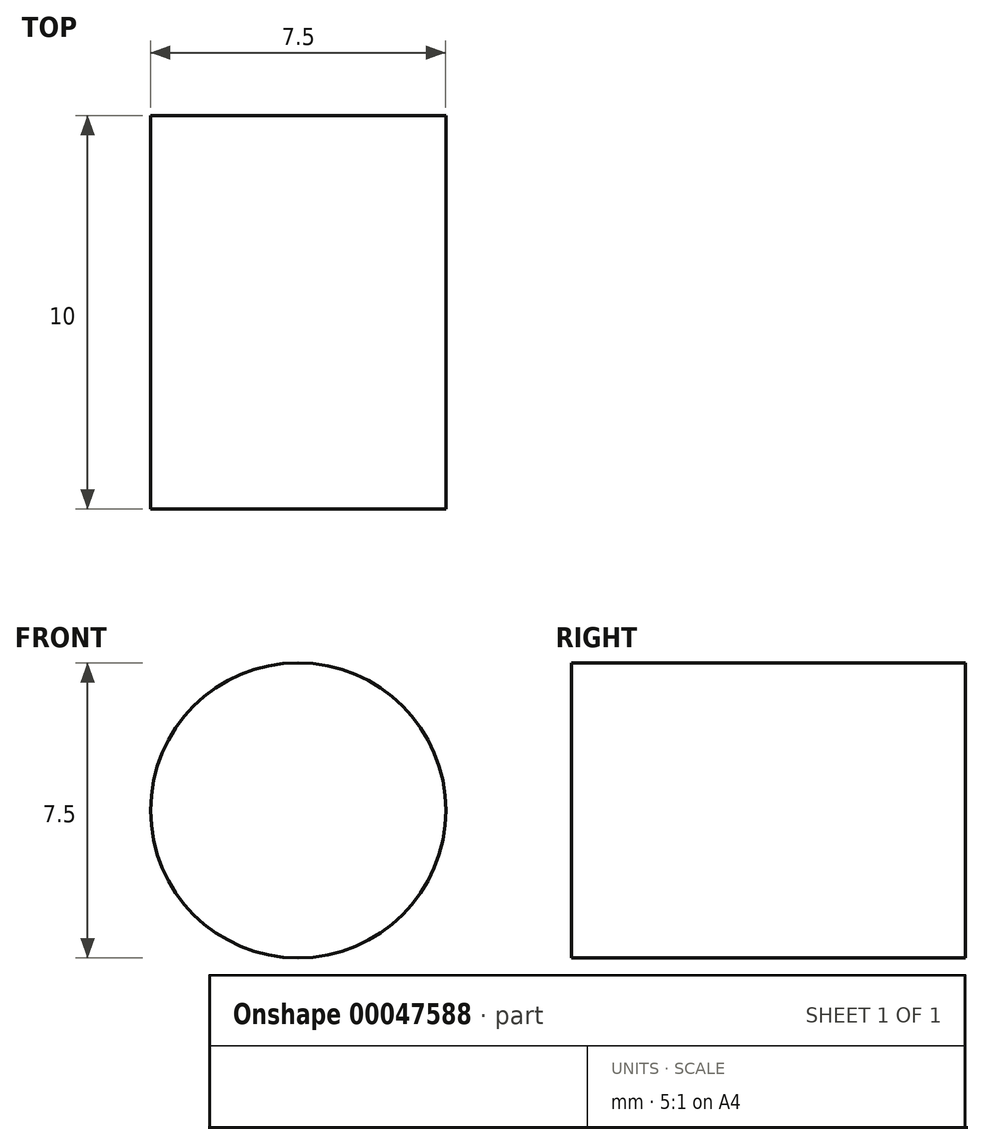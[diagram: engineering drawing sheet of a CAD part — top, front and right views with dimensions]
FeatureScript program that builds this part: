
annotation { "Feature Type Name" : "Feature", "Feature Type Description" : "" }
export const myFeature = defineFeature(function(context is Context, id is Id, definition is map)
    precondition{}
    {
        {
            var Q0;
            Q0=qCreatedBy(makeId("Front.planeOp"),FACE);
            var sketch = newSketch(context, id + "F0", { "sketchPlane" : qUnion([Q0])});
            skCircle(sketch, "E0", {"center": v(-48.09, 23.9) * mm, "radius": 3.75 * mm});
            skSolve(sketch);
        }
        {
            var Q0;
            Q0=makeQuery(id+"F0.imprint","IMPRINT",FACE,{"disambiguationData":[TD([[makeQuery(id+"F0.imprint","IMPRINT",EDGE,{"derivedFrom":sQuery(id+"F0.wireOp",EDGE,"E0")}),1.0]])]});
            extrude(context, id + "F1", {"entities" : qUnion([Q0]), "depth" : 10 * mm});
        }
    });
